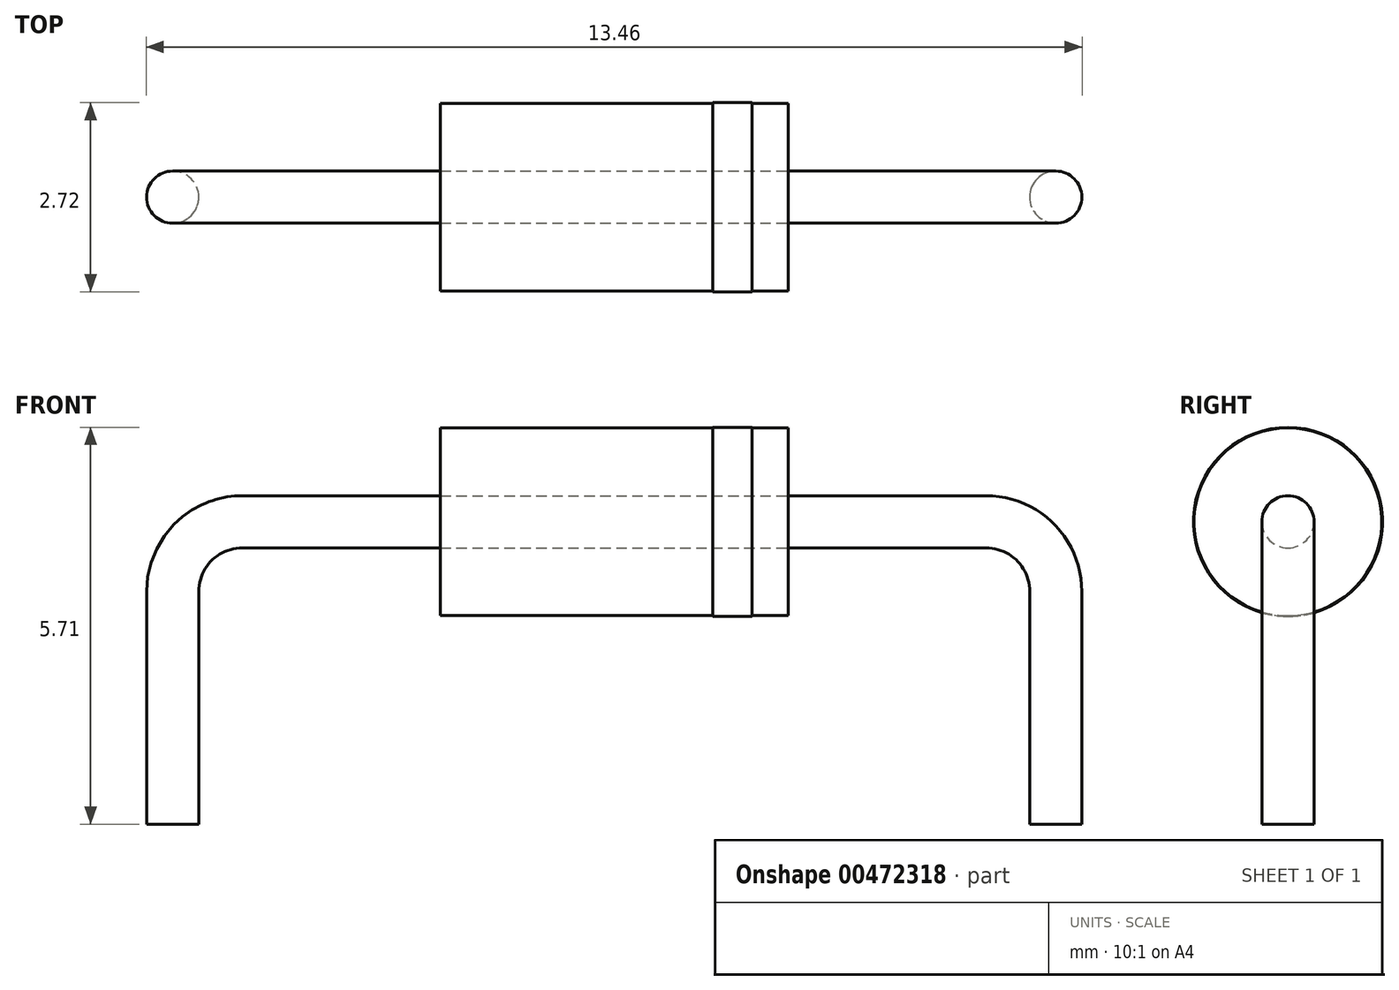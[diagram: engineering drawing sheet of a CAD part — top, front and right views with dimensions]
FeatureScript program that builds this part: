
annotation { "Feature Type Name" : "Feature", "Feature Type Description" : "" }
export const myFeature = defineFeature(function(context is Context, id is Id, definition is map)
    precondition{}
    {
        {
            var Q0;
            Q0=qCreatedBy(makeId("Front.planeOp"),FACE);
            var sketch = newSketch(context, id + "F0", { "sketchPlane" : qUnion([Q0])});
            skLineSegment(sketch, "E0", {"start": v(-6.35, 0) * mm, "end": v(-6.35, 3.35) * mm});
            skLineSegment(sketch, "E1", {"start": v(-5.35, 4.35) * mm, "end": v(5.35, 4.35) * mm});
            skLineSegment(sketch, "E2", {"start": v(6.35, 3.35) * mm, "end": v(6.35, 0) * mm});
            skPoint(sketch, "E3.visualSharp", {"position": v(-6.35, 4.35) * mm});
            skArc(sketch, "E3.filletArc", {"start": v(-5.35, 4.35) * mm, "mid": v(-6.06, 4.06) * mm, "end": v(-6.35, 3.35) * mm});
            skPoint(sketch, "E4.visualSharp", {"position": v(6.35, 4.35) * mm});
            skArc(sketch, "E4.filletArc", {"start": v(6.35, 3.35) * mm, "mid": v(6.06, 4.06) * mm, "end": v(5.35, 4.35) * mm});
            skSolve(sketch);
        }
        {
            var Q0;
            Q0=qCreatedBy(makeId("Top.planeOp"),FACE);
            var sketch = newSketch(context, id + "F1", { "sketchPlane" : qUnion([Q0])});
            skCircle(sketch, "E5", {"center": v(-6.35, 0) * mm, "radius": 0.38 * mm});
            skSolve(sketch);
        }
        {
            var Q0;
            Q0 = qSketchRegion(id + "F1", true);
            var Q1;
            Q1 = qConstructionFilter(qBodyType(qCreatedBy(id + "F0" ,EDGE), BodyType.WIRE), ConstructionObject.NO);
            sweep(context, id + "F2", {"profiles" : qUnion([Q0]), "path" : qUnion([Q1])});
        }
        {
            var Q0;
            Q0=qCreatedBy(makeId("Right.planeOp"),FACE);
            var sketch = newSketch(context, id + "F3", { "sketchPlane" : qUnion([Q0])});
            skCircle(sketch, "E6", {"center": v(0, 4.35) * mm, "radius": 1.35 * mm});
            skSolve(sketch);
        }
        {
            var Q0;
            Q0=makeQuery(id+"F3.imprint","IMPRINT",FACE,{"disambiguationData":[TD([[makeQuery(id+"F3.imprint","IMPRINT",EDGE,{"derivedFrom":sQuery(id+"F3.wireOp",EDGE,"E6")}),1.0]])]});
            extrude(context, id + "F4", {"entities" : qUnion([Q0]), "oppositeDirection" : true, "depth" : 2.5 * mm, "hasSecondDirection" : true, "secondDirectionOppositeDirection" : false, "secondDirectionDepth" : 2.5 * mm});
        }
        {
            var Q0;
            Q0=makeQuery(id+"F4.opExtrude","CAP_FACE",FACE,{"disambiguationData":[OSD([sQuery(id+"F3.wireOp",EDGE,"E6")])],"isStart":true});
            var sketch = newSketch(context, id + "F5", { "sketchPlane" : qUnion([Q0])});
            skCircle(sketch, "E7", {"center": v(0, 4.35) * mm, "radius": 1.36 * mm});
            skSolve(sketch);
        }
        {
            var Q0;
            Q0 = qSketchRegion(id + "F5", true);
            extrude(context, id + "F6", {"entities" : qUnion([Q0]), "oppositeDirection" : true, "depth" : 1.08 * mm, "hasSecondDirection" : true, "secondDirectionOppositeDirection" : true, "secondDirectionDepth" : 0.52 * mm});
        }
    });
